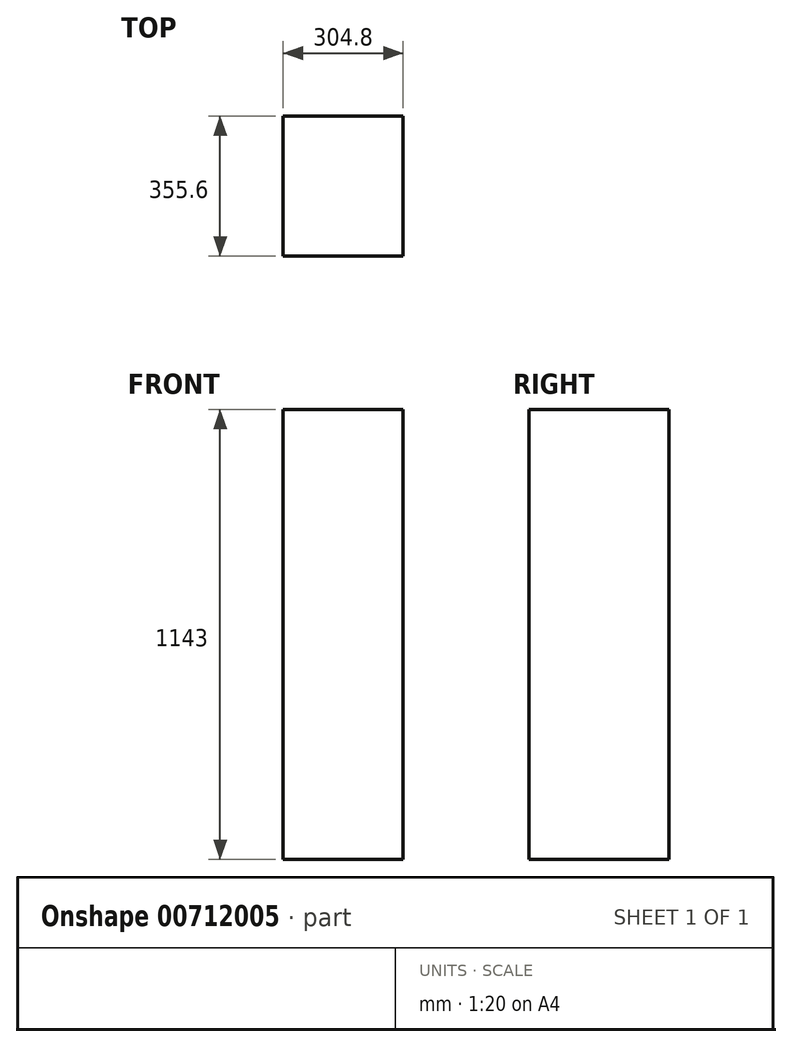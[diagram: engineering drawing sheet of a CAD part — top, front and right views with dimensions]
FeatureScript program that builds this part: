
annotation { "Feature Type Name" : "Feature", "Feature Type Description" : "" }
export const myFeature = defineFeature(function(context is Context, id is Id, definition is map)
    precondition{}
    {
        {
            var Q0;
            Q0=qCreatedBy(makeId("Front.planeOp"),FACE);
            var sketch = newSketch(context, id + "F0", { "sketchPlane" : qUnion([Q0])});
            skLineSegment(sketch, "E0.bottom", {"start": v(-152.4, 589) * mm, "end": v(152.4, 589) * mm});
            skLineSegment(sketch, "E0.top", {"start": v(-152.4, -554) * mm, "end": v(152.4, -554) * mm});
            skLineSegment(sketch, "E0.left", {"start": v(-152.4, 589) * mm, "end": v(-152.4, -554) * mm});
            skLineSegment(sketch, "E0.right", {"start": v(152.4, 589) * mm, "end": v(152.4, -554) * mm});
            skPoint(sketch, "E0.middle", {"position": v(0, 17.5) * mm});
            skSolve(sketch);
        }
        {
            var Q0;
            Q0 = qSketchRegion(id + "F0", true);
            extrude(context, id + "F1", {"entities" : qUnion([Q0]), "depth" : 355.6 * mm, "offsetDistance" : 25.4 * mm});
        }
    });
